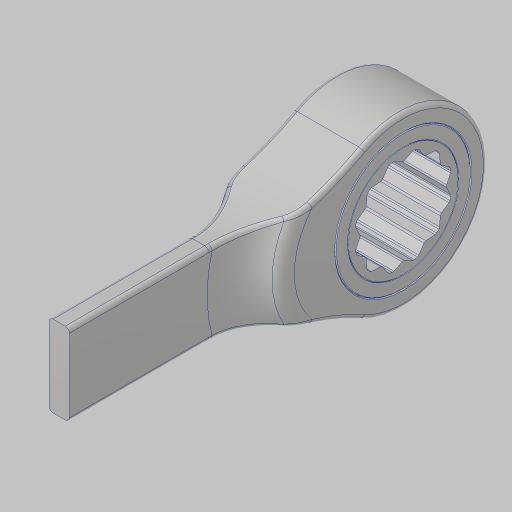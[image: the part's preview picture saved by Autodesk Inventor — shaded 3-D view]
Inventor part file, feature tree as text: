
AUTODESK INVENTOR PART (.ipt)
format: ipt  version: 2023.5 (Build 275446000, 446)  size: 386,048 bytes
history: native  units: in
note: dims shown in document units (in); Inventor stores cm internally (conversion verified against a paired STEP export)
features: fillet x2, extrude x1, sketch x1
ambient origin geometry x8: Origin, YZ Plane, XZ Plane, XY Plane, X Axis, Y Axis, Z Axis, Center Point
bodies: Solid1 (feature_tree), Solid2 (feature_tree)
feature tree (4):
  extrude  "Extrusion1"  [1 undecoded]
  sketch  "Sketch1"  dims[d0=1.0in d1=0.0in]
  fillet  "Fillet4"  [1 undecoded]
  fillet  "Fillet2"  [1 undecoded]
note: 3 required parameter values undecoded (feature->parameter linkage not recoverable at this tier; creation-order binding heuristic only, values carry confidence <= 0.55)
